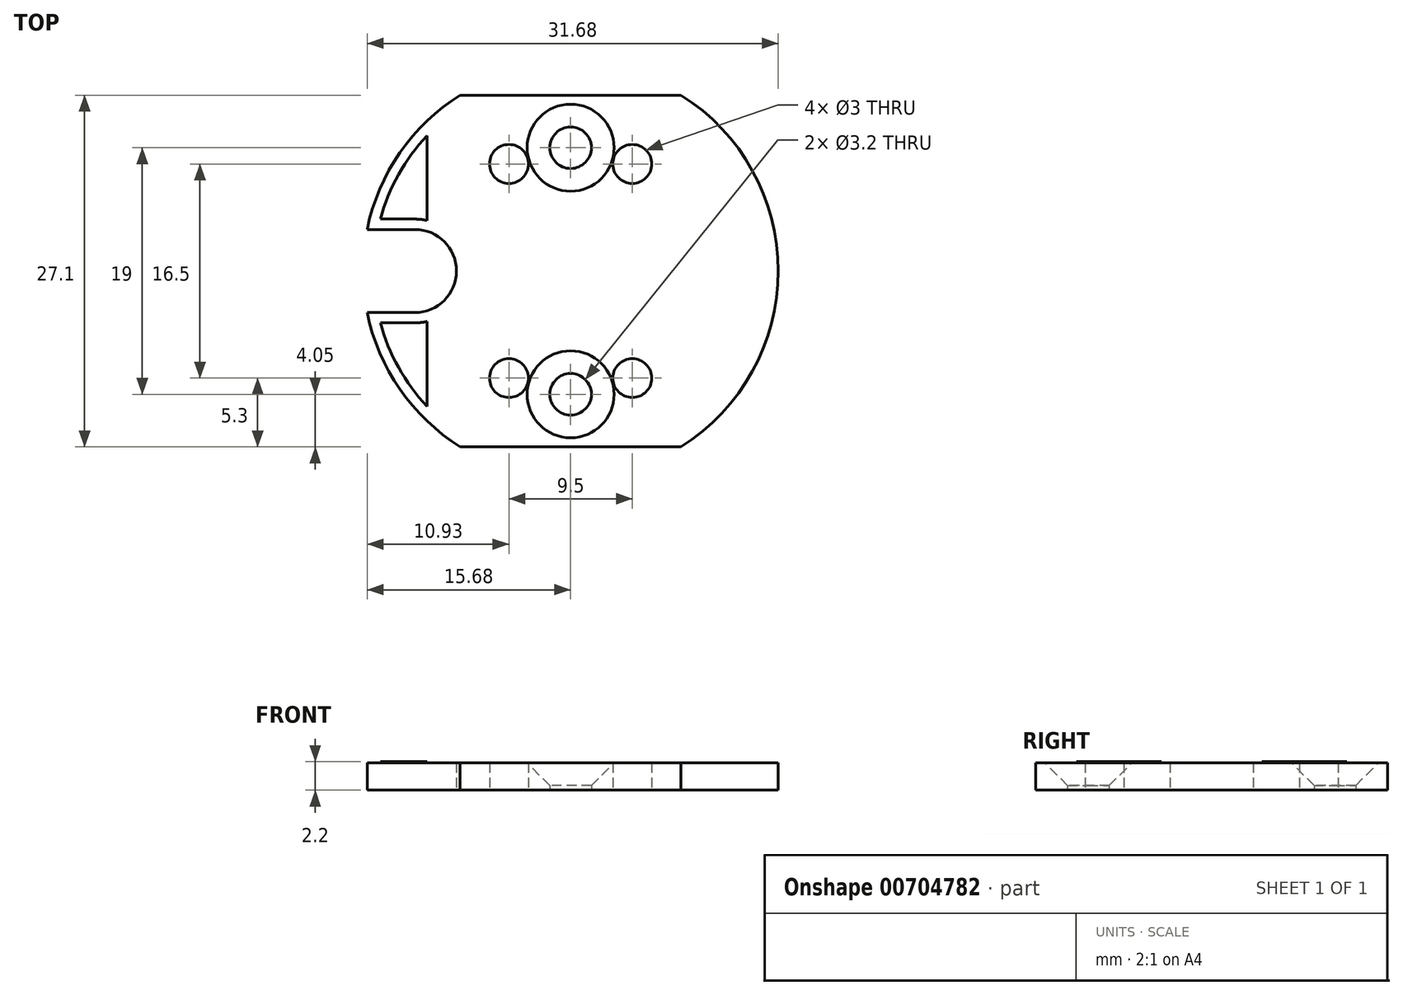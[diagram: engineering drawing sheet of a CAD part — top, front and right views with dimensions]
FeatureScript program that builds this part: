
annotation { "Feature Type Name" : "Feature", "Feature Type Description" : "" }
export const myFeature = defineFeature(function(context is Context, id is Id, definition is map)
    precondition{}
    {
        {
            var Q0;
            Q0=qCreatedBy(makeId("Top.planeOp"),FACE);
            var sketch = newSketch(context, id + "F0", { "sketchPlane" : qUnion([Q0])});
            skArc(sketch, "E0", {"start": v(-8.5, 13.55) * mm, "mid": v(-13.15, 9.1) * mm, "end": v(-15.68, 3.2) * mm});
            skLineSegment(sketch, "E1.bottom", {"start": v(8.5, 13.55) * mm, "end": v(-8.5, 13.55) * mm});
            skLineSegment(sketch, "E1.top", {"start": v(8.5, -13.55) * mm, "end": v(-8.5, -13.55) * mm});
            skPoint(sketch, "E2.orphan", {"position": v(13.55, 13.55) * mm});
            skPoint(sketch, "E3.orphan", {"position": v(-13.55, 13.55) * mm});
            skPoint(sketch, "E4.orphan", {"position": v(-13.55, -13.55) * mm});
            skArc(sketch, "E5.trimOffspring", {"start": v(8.5, -13.55) * mm, "mid": v(16, 0) * mm, "end": v(8.5, 13.55) * mm});
            skPoint(sketch, "E6.orphan", {"position": v(13.55, -13.55) * mm});
            skArc(sketch, "E7", {"start": v(-12, -3.2) * mm, "mid": v(-8.8, 0) * mm, "end": v(-12, 3.2) * mm});
            skLineSegment(sketch, "E8", {"start": v(-12, 3.2) * mm, "end": v(-15.68, 3.2) * mm});
            skLineSegment(sketch, "E9", {"start": v(-12, -3.2) * mm, "end": v(-15.68, -3.2) * mm});
            skArc(sketch, "E10.trimOffspring", {"start": v(-15.68, -3.2) * mm, "mid": v(-13.15, -9.1) * mm, "end": v(-8.5, -13.55) * mm});
            skCircle(sketch, "E11", {"center": v(-4.75, 8.25) * mm, "radius": 1.5 * mm});
            skCircle(sketch, "E12", {"center": v(4.75, 8.25) * mm, "radius": 1.5 * mm});
            skCircle(sketch, "E13", {"center": v(4.75, -8.25) * mm, "radius": 1.5 * mm});
            skCircle(sketch, "E14", {"center": v(-4.75, -8.25) * mm, "radius": 1.5 * mm});
            skLineSegment(sketch, "E15", {"start": v(0, -13.55) * mm, "end": v(0, -9.5) * mm});
            skCircle(sketch, "E16", {"center": v(0, -9.5) * mm, "radius": 1.6 * mm});
            skLineSegment(sketch, "E17", {"start": v(-8.8, 0) * mm, "end": v(-5.89, 0) * mm});
            skCircle(sketch, "E18.MirrorC", {"center": v(0, 9.5) * mm, "radius": 1.6 * mm});
            skSolve(sketch);
        }
        {
            var Q0;
            Q0=makeQuery(id+"F0.imprint","IMPRINT",FACE,{"disambiguationData":[TD([[makeQuery(id+"F0.imprint","IMPRINT",EDGE,{"derivedFrom":sQuery(id+"F0.wireOp",EDGE,"E0")}),1.0]])]});
            extrude(context, id + "F1", {"entities" : qUnion([Q0]), "depth" : 2.1 * mm, "offsetDistance" : 25 * mm});
        }
        {
            var Q0;
            Q0=makeQuery(id+"F1.opExtrude","CAP_EDGE",EDGE,{"disambiguationData":[OSD([sQuery(id+"F0.wireOp",EDGE,"E16")])],"isStart":false});
            var Q1;
            Q1=makeQuery(id+"F1.opExtrude","CAP_EDGE",EDGE,{"disambiguationData":[OSD([sQuery(id+"F0.wireOp",EDGE,"E18.MirrorC")])],"isStart":false});
            chamfer(context, id + "F2", {"entities" : qUnion([Q0, Q1]), "width" : 1.75 * mm, "tangentPropagation" : true});
        }
        {
            var Q0;
            Q0=makeQuery(id+"F1.opExtrude","CAP_FACE",FACE,{"disambiguationData":[OSD([sQuery(id+"F0.wireOp",EDGE,"E0"),sQuery(id+"F0.wireOp",EDGE,"E1.bottom"),sQuery(id+"F0.wireOp",EDGE,"E1.top"),sQuery(id+"F0.wireOp",EDGE,"E5.trimOffspring"),sQuery(id+"F0.wireOp",EDGE,"E7"),sQuery(id+"F0.wireOp",EDGE,"E8"),sQuery(id+"F0.wireOp",EDGE,"E9"),sQuery(id+"F0.wireOp",EDGE,"E10.trimOffspring"),sQuery(id+"F0.wireOp",EDGE,"E11"),sQuery(id+"F0.wireOp",EDGE,"E12"),sQuery(id+"F0.wireOp",EDGE,"E13"),sQuery(id+"F0.wireOp",EDGE,"E14"),sQuery(id+"F0.wireOp",EDGE,"E16"),sQuery(id+"F0.wireOp",EDGE,"E18.MirrorC")])],"isStart":false});
            var sketch = newSketch(context, id + "F3", { "sketchPlane" : qUnion([Q0])});
            skArc(sketch, "E19.0", {"start": v(-14.66, -4) * mm, "mid": v(-12.28, -8.96) * mm, "end": v(-8.28, -12.75) * mm});
            skLineSegment(sketch, "E19.1", {"start": v(-12, -4) * mm, "end": v(-14.66, -4) * mm});
            skLineSegment(sketch, "E19.2", {"start": v(-8.28, -12.75) * mm, "end": v(8.28, -12.75) * mm});
            skArc(sketch, "E19.3", {"start": v(-12, 4) * mm, "mid": v(-8, 0) * mm, "end": v(-12, -4) * mm});
            skArc(sketch, "E19.4", {"start": v(8.28, -12.75) * mm, "mid": v(15.2, 0) * mm, "end": v(8.28, 12.75) * mm});
            skLineSegment(sketch, "E19.5", {"start": v(8.28, 12.75) * mm, "end": v(-8.28, 12.75) * mm});
            skArc(sketch, "E19.6", {"start": v(-8.28, 12.75) * mm, "mid": v(-12.28, 8.96) * mm, "end": v(-14.66, 4) * mm});
            skLineSegment(sketch, "E19.7", {"start": v(-14.66, 4) * mm, "end": v(-12, 4) * mm});
            skLineSegment(sketch, "E20", {"start": v(-11.07, 10.42) * mm, "end": v(-11.07, -10.42) * mm});
            skSolve(sketch);
        }
        {
            var Q0;
            {var subQ0=sQuery(id+"F3.wireOp",EDGE,"E19.7");Q0=makeQuery(id+"F3.imprint","IMPRINT",FACE,{"disambiguationData":[TD([[makeQuery(id+"F3.imprint","IMPRINT",EDGE,{"derivedFrom":subQ0}),1.0]])]});}
            var Q1;
            {var subQ0=sQuery(id+"F3.wireOp",EDGE,"E19.1");Q1=makeQuery(id+"F3.imprint","IMPRINT",FACE,{"disambiguationData":[TD([[makeQuery(id+"F3.imprint","IMPRINT",EDGE,{"derivedFrom":subQ0}),1.0]])]});}
            extrude(context, id + "F4", {"entities" : qUnion([Q0, Q1]), "operationType" : NewBodyOperationType.ADD, "depth" : .1 * mm, "offsetDistance" : 25 * mm});
        }
    });
